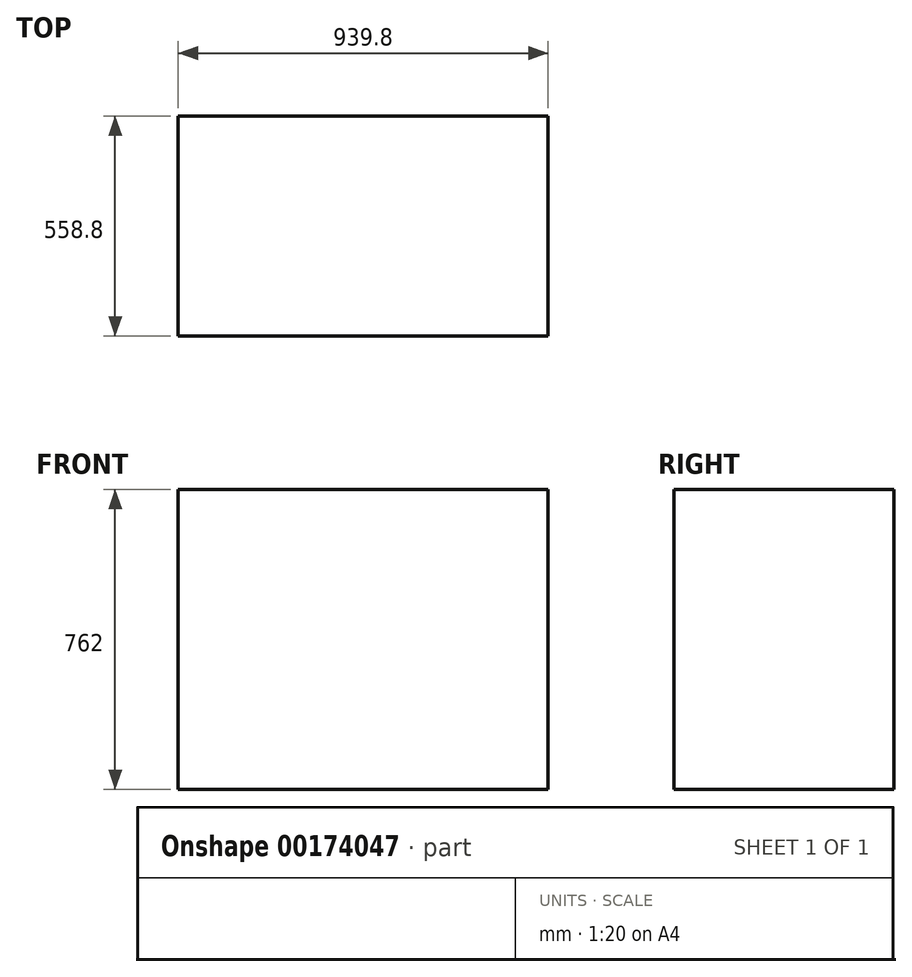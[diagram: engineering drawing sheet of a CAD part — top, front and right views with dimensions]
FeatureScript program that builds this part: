
annotation { "Feature Type Name" : "Feature", "Feature Type Description" : "" }
export const myFeature = defineFeature(function(context is Context, id is Id, definition is map)
    precondition{}
    {
        {
            var Q0;
            Q0=qCreatedBy(makeId("Top.planeOp"),FACE);
            var sketch = newSketch(context, id + "F0", { "sketchPlane" : qUnion([Q0])});
            skLineSegment(sketch, "E0.bottom", {"start": v(469.9, 279.4) * mm, "end": v(-469.9, 279.4) * mm});
            skLineSegment(sketch, "E0.top", {"start": v(469.9, -279.4) * mm, "end": v(-469.9, -279.4) * mm});
            skLineSegment(sketch, "E0.left", {"start": v(469.9, 279.4) * mm, "end": v(469.9, -279.4) * mm});
            skLineSegment(sketch, "E0.right", {"start": v(-469.9, 279.4) * mm, "end": v(-469.9, -279.4) * mm});
            skPoint(sketch, "E0.middle", {"position": v(0, 0) * mm});
            skSolve(sketch);
        }
        {
            var Q0;
            Q0=makeQuery(id+"F0.imprint","IMPRINT",FACE,{"disambiguationData":[TD([[makeQuery(id+"F0.imprint","IMPRINT",EDGE,{"derivedFrom":sQuery(id+"F0.wireOp",EDGE,"E0.bottom")}),1.0]])]});
            extrude(context, id + "F1", {"entities" : qUnion([Q0]), "depth" : 762 * mm});
        }
    });
